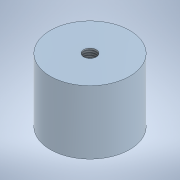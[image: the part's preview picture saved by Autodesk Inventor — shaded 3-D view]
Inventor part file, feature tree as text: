
AUTODESK INVENTOR PART (.ipt)
format: ipt  version: 2022 (Build 260153000, 153)  size: 99,328 bytes
history: native  units: in
note: dims shown in document units (in); Inventor stores cm internally (conversion verified against a paired STEP export)
features: sketch x2, extrude x1, hole x1, thread x1
ambient origin geometry x8: Origin, YZ Plane, XZ Plane, XY Plane, X Axis, Y Axis, Z Axis, Center Point
bodies: Solid1 (feature_tree)
feature tree (5):
  extrude  "Extrusion1"  Depth=0.7874in TaperAngle=0.0deg
  hole  "Hole1"  [1 undecoded]
  thread  "Thread1"  [1 undecoded]
  sketch  "Sketch1"  dims[d0=0.9843in d1=0.7874in d2=0.0in]
  sketch  "Sketch2"  dims[d3=0.1575in d4=0.2362in d5=1.0039in d6=0.0591in d7=90.0deg d8=0.315in d9=0.8108in d10=0.7874in d11=0.0in]
note: 2 required parameter values undecoded (feature->parameter linkage not recoverable at this tier; creation-order binding heuristic only, values carry confidence <= 0.55)
